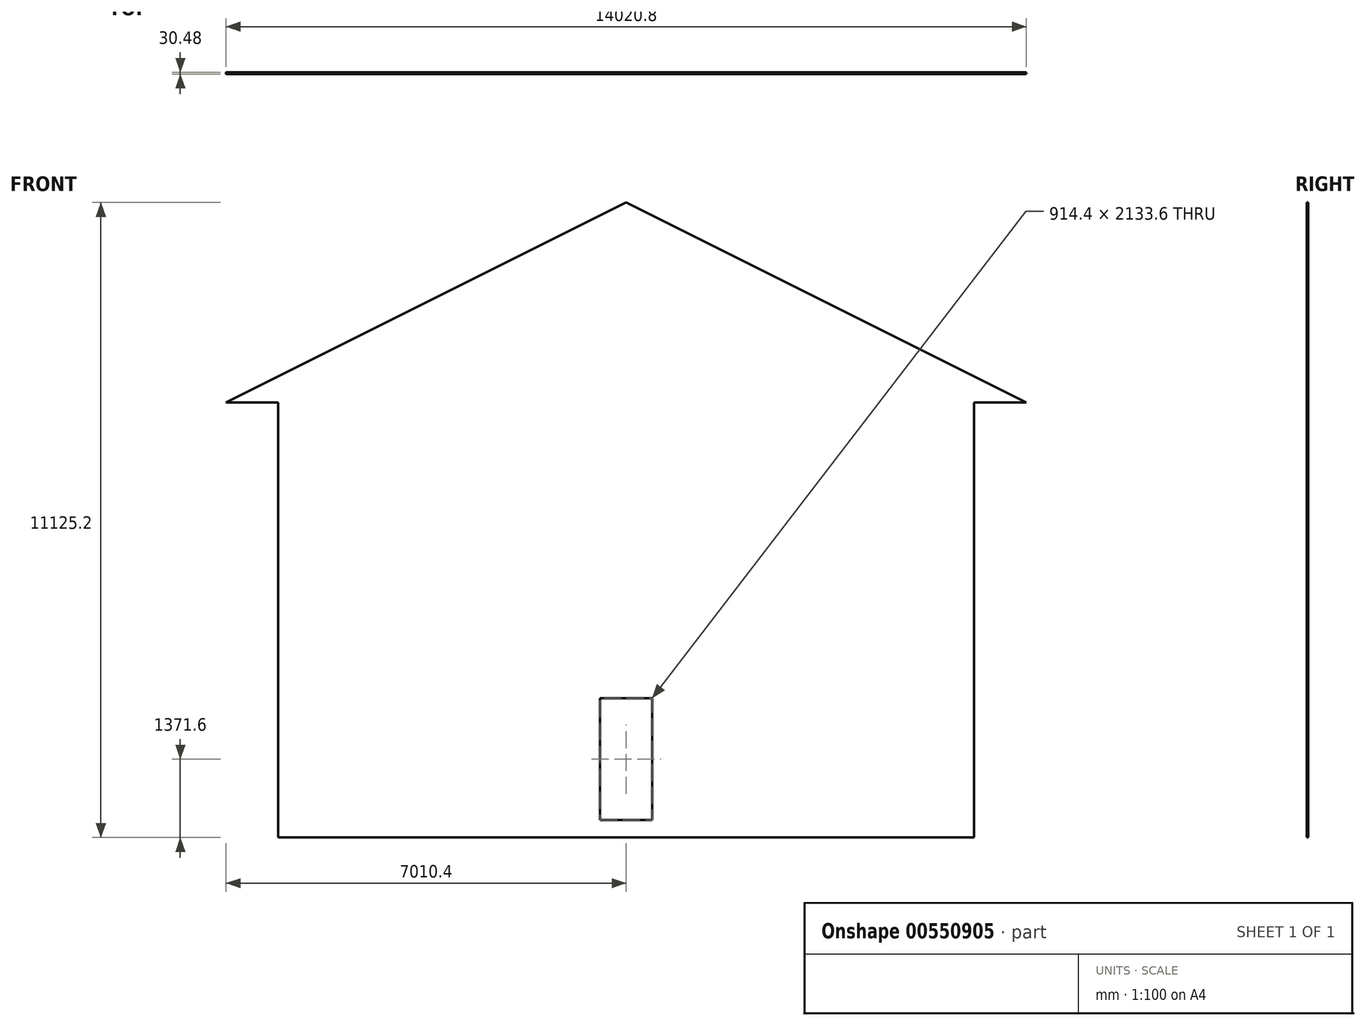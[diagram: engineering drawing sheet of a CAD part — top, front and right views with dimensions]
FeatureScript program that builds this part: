
annotation { "Feature Type Name" : "Feature", "Feature Type Description" : "" }
export const myFeature = defineFeature(function(context is Context, id is Id, definition is map)
    precondition{}
    {
        {
            var Q0;
            Q0=qCreatedBy(makeId("Front.planeOp"),FACE);
            var sketch = newSketch(context, id + "F0", { "sketchPlane" : qUnion([Q0])});
            skLineSegment(sketch, "E0", {"start": v(0, 0) * mm, "end": v(-6096, 0) * mm});
            skLineSegment(sketch, "E1", {"start": v(0, 0) * mm, "end": v(6096, 0) * mm});
            skLineSegment(sketch, "E2", {"start": v(-6096, 0) * mm, "end": v(-7010.4, 0) * mm});
            skLineSegment(sketch, "E3", {"start": v(0, 0) * mm, "end": v(0, 3048) * mm});
            skLineSegment(sketch, "E4", {"start": v(0, 3048) * mm, "end": v(-6096, 0) * mm});
            skLineSegment(sketch, "E5", {"start": v(0, 3048) * mm, "end": v(6096, 0) * mm});
            skLineSegment(sketch, "E6", {"start": v(0, 3048) * mm, "end": v(0, 3505.2) * mm});
            skLineSegment(sketch, "E7", {"start": v(-7010.4, 0) * mm, "end": v(0, 3505.2) * mm});
            skLineSegment(sketch, "E8", {"start": v(6096, 0) * mm, "end": v(7010.4, 0) * mm});
            skLineSegment(sketch, "E9", {"start": v(0, 3505.2) * mm, "end": v(7010.4, 0) * mm});
            skLineSegment(sketch, "E10", {"start": v(-6096, 0) * mm, "end": v(-6096, -7315.2) * mm});
            skLineSegment(sketch, "E11", {"start": v(6096, 0) * mm, "end": v(6096, -7315.2) * mm});
            skLineSegment(sketch, "E12", {"start": v(-6096, -7315.2) * mm, "end": v(6096, -7315.2) * mm});
            skLineSegment(sketch, "E13", {"start": v(6096, -7315.2) * mm, "end": v(6096, -7620) * mm});
            skLineSegment(sketch, "E14", {"start": v(-6096, -7315.2) * mm, "end": v(-6096, -7620) * mm});
            skLineSegment(sketch, "E15", {"start": v(-6096, -7620) * mm, "end": v(6096, -7620) * mm});
            skPoint(sketch, "E16.endSnap0", {"position": v(0, -7315.2) * mm});
            skLineSegment(sketch, "E17", {"start": v(0, -7315.2) * mm, "end": v(-457.2, -7315.2) * mm});
            skLineSegment(sketch, "E18", {"start": v(-457.2, -7315.2) * mm, "end": v(-457.2, -5181.6) * mm});
            skLineSegment(sketch, "E19", {"start": v(-457.2, -5181.6) * mm, "end": v(457.2, -5181.6) * mm});
            skLineSegment(sketch, "E20", {"start": v(457.2, -5181.6) * mm, "end": v(457.2, -7315.2) * mm});
            skSolve(sketch);
        }
        {
            var Q0;
            Q0=makeQuery(id+"F0.imprint","IMPRINT",FACE,{"disambiguationData":[TD([[makeQuery(id+"F0.imprint","IMPRINT",EDGE,{"derivedFrom":sQuery(id+"F0.wireOp",EDGE,"E0")}),1.0]])]});
            var Q1;
            Q1=makeQuery(id+"F0.imprint","IMPRINT",FACE,{"disambiguationData":[TD([[makeQuery(id+"F0.imprint","IMPRINT",EDGE,{"derivedFrom":sQuery(id+"F0.wireOp",EDGE,"E2")}),-1.0]])]});
            var Q2;
            Q2=makeQuery(id+"F0.imprint","IMPRINT",FACE,{"disambiguationData":[TD([[makeQuery(id+"F0.imprint","IMPRINT",EDGE,{"derivedFrom":sQuery(id+"F0.wireOp",EDGE,"E5")}),1.0]])]});
            var Q3;
            Q3=makeQuery(id+"F0.imprint","IMPRINT",FACE,{"disambiguationData":[TD([[makeQuery(id+"F0.imprint","IMPRINT",EDGE,{"derivedFrom":sQuery(id+"F0.wireOp",EDGE,"E1")}),1.0]])]});
            var Q4;
            Q4=makeQuery(id+"F0.imprint","IMPRINT",FACE,{"disambiguationData":[TD([[makeQuery(id+"F0.imprint","IMPRINT",EDGE,{"derivedFrom":sQuery(id+"F0.wireOp",EDGE,"E0")}),-1.0]])]});
            var Q5;
            {var subQ0=sQuery(id+"F0.wireOp",EDGE,"E17");Q5=makeQuery(id+"F0.imprint","IMPRINT",FACE,{"disambiguationData":[TD([[makeQuery(id+"F0.imprint","IMPRINT",EDGE,{"derivedFrom":subQ0}),-1.0]])]});}
            var Q6;
            {var subQ0=sQuery(id+"F0.wireOp",EDGE,"E13");Q6=makeQuery(id+"F0.imprint","IMPRINT",FACE,{"disambiguationData":[TD([[makeQuery(id+"F0.imprint","IMPRINT",EDGE,{"derivedFrom":subQ0}),-1.0]])]});}
            extrude(context, id + "F1", {"entities" : qUnion([Q0, Q1, Q2, Q3, Q4, Q5, Q6]), "depth" : 30.48 * mm, "offsetDistance" : 30.48 * mm});
        }
    });
